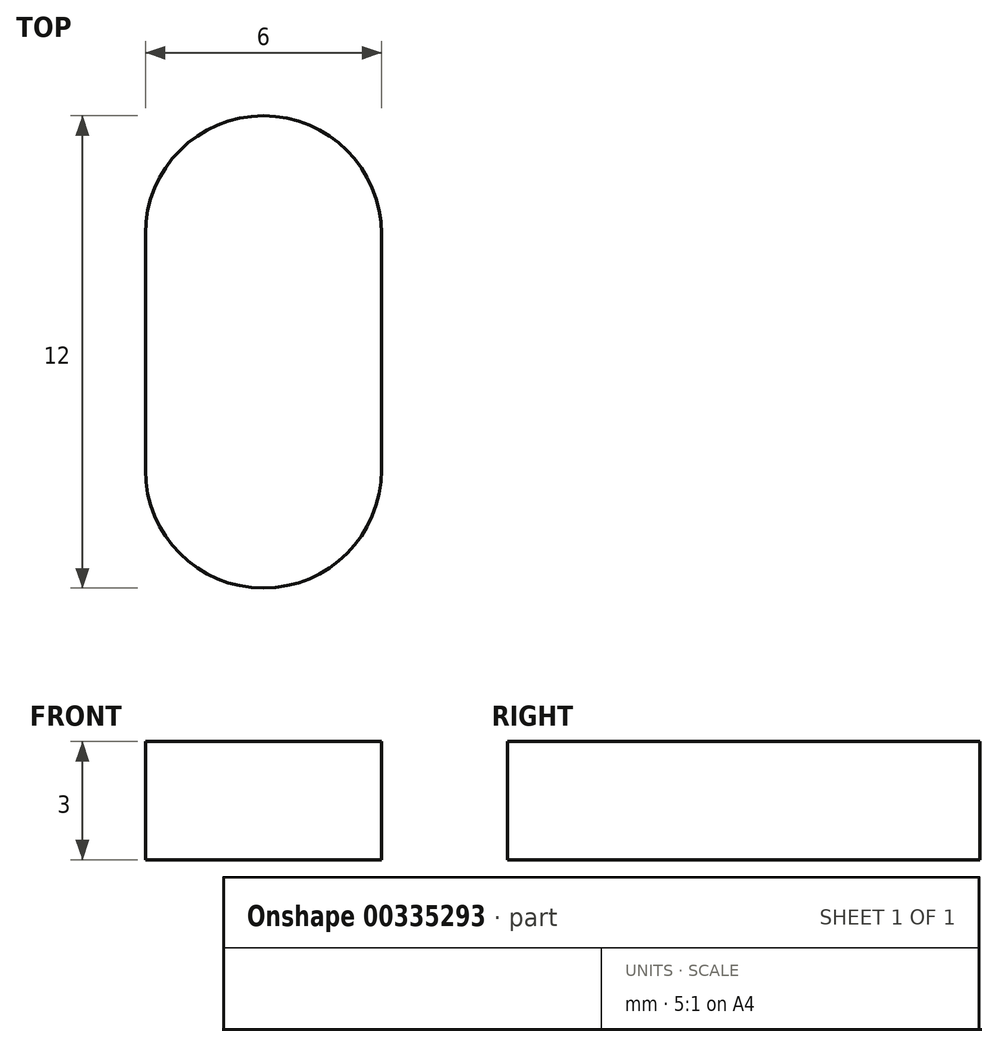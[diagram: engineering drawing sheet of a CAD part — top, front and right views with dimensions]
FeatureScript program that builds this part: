
annotation { "Feature Type Name" : "Feature", "Feature Type Description" : "" }
export const myFeature = defineFeature(function(context is Context, id is Id, definition is map)
    precondition{}
    {
        {
            var Q0;
            Q0=qCreatedBy(makeId("Top.planeOp"),FACE);
            var sketch = newSketch(context, id + "F0", { "sketchPlane" : qUnion([Q0])});
            skCircle(sketch, "E0", {"center": v(0, 3) * mm, "radius": 3 * mm});
            skCircle(sketch, "E1", {"center": v(0, -3) * mm, "radius": 3 * mm});
            skLineSegment(sketch, "E2", {"start": v(3, 3) * mm, "end": v(3, -3) * mm});
            skLineSegment(sketch, "E3", {"start": v(-3, 3) * mm, "end": v(-3, -3) * mm});
            skSolve(sketch);
        }
        {
            var Q0;
            {var subQ0=sQuery(id+"F0.wireOp",EDGE,"E3");Q0=makeQuery(id+"F0.imprint","IMPRINT",FACE,{"disambiguationData":[TD([[makeQuery(id+"F0.imprint","IMPRINT",EDGE,{"derivedFrom":subQ0}),1.0]])]});}
            var Q1;
            {var subQ0=sQuery(id+"F0.wireOp",EDGE,"E2");Q1=makeQuery(id+"F0.imprint","IMPRINT",FACE,{"disambiguationData":[TD([[makeQuery(id+"F0.imprint","IMPRINT",EDGE,{"derivedFrom":subQ0}),-1.0]])]});}
            var Q2;
            {var subQ0=sQuery(id+"F0.wireOp",EDGE,"E0");var subQ1=makeQuery(id+"F0.imprint","INTERSECT",VERTEX,{"derivedFrom":[subQ0,sQuery(id+"F0.wireOp",EDGE,"E2")]});Q2=makeQuery(id+"F0.imprint","IMPRINT",FACE,{"disambiguationData":[TD([[makeQuery(id+"F0.imprint","IMPRINT",EDGE,{"disambiguationData":[TD([[subQ1,-1.0]])],"derivedFrom":subQ0}),1.0]])]});}
            var Q3;
            {var subQ0=sQuery(id+"F0.wireOp",EDGE,"E1");var subQ1=makeQuery(id+"F0.imprint","INTERSECT",VERTEX,{"derivedFrom":[subQ0,sQuery(id+"F0.wireOp",EDGE,"E2")]});Q3=makeQuery(id+"F0.imprint","IMPRINT",FACE,{"disambiguationData":[TD([[makeQuery(id+"F0.imprint","IMPRINT",EDGE,{"disambiguationData":[TD([[subQ1,-1.0]])],"derivedFrom":subQ0}),1.0]])]});}
            extrude(context, id + "F1", {"entities" : qUnion([Q0, Q1, Q2, Q3]), "depth" : 3 * mm, "symmetric" : true});
        }
    });
